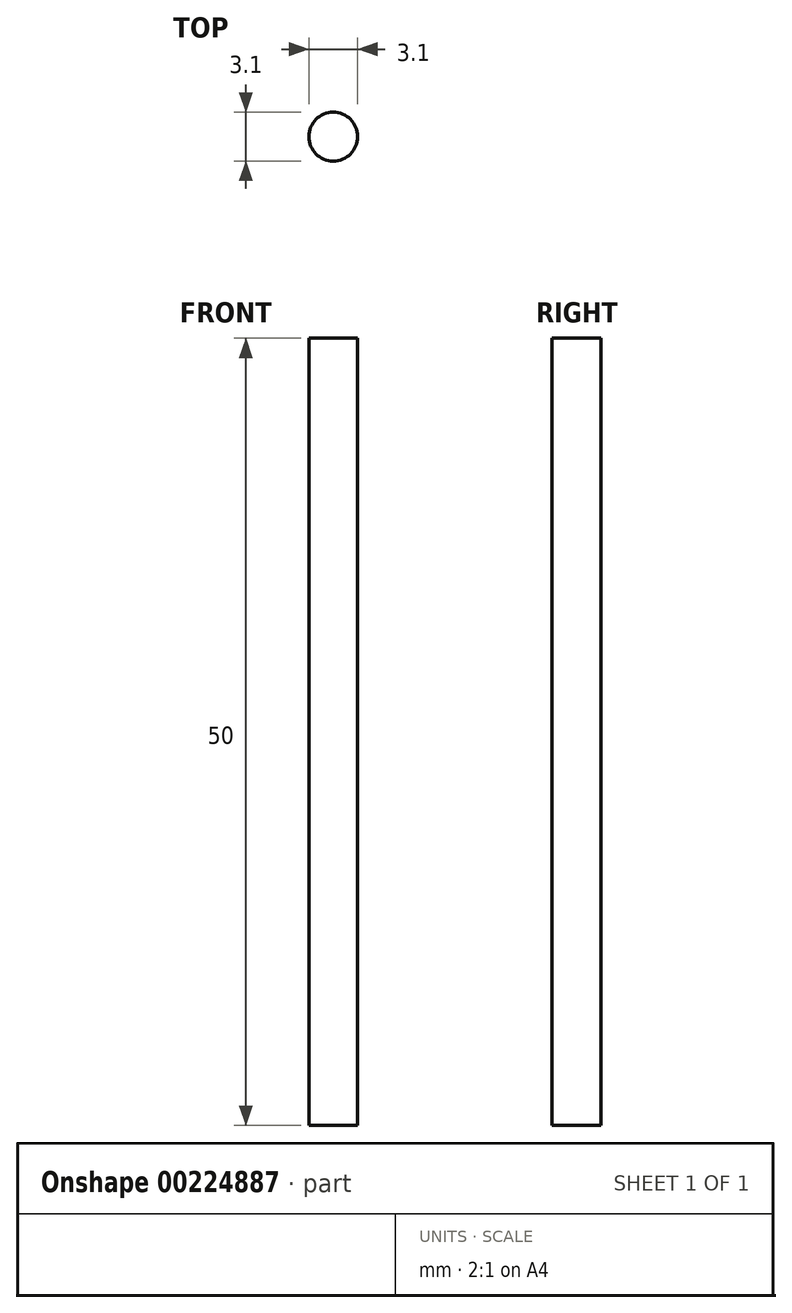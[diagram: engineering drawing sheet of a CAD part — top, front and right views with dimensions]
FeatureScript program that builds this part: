
annotation { "Feature Type Name" : "Feature", "Feature Type Description" : "" }
export const myFeature = defineFeature(function(context is Context, id is Id, definition is map)
    precondition{}
    {
        {
            var Q0;
            Q0=qCreatedBy(makeId("Top.planeOp"),FACE);
            var sketch = newSketch(context, id + "F0", { "sketchPlane" : qUnion([Q0])});
            skCircle(sketch, "E0", {"center": v(0, 0) * mm, "radius": 1.55 * mm});
            skSolve(sketch);
        }
        {
            var Q0;
            Q0=makeQuery(id+"F0.imprint","IMPRINT",FACE,{"disambiguationData":[TD([[makeQuery(id+"F0.imprint","IMPRINT",EDGE,{"derivedFrom":sQuery(id+"F0.wireOp",EDGE,"E0")}),1.0]])]});
            extrude(context, id + "F1", {"entities" : qUnion([Q0]), "endBound" : BoundingType.SYMMETRIC, "depth" : 50 * mm});
        }
    });
